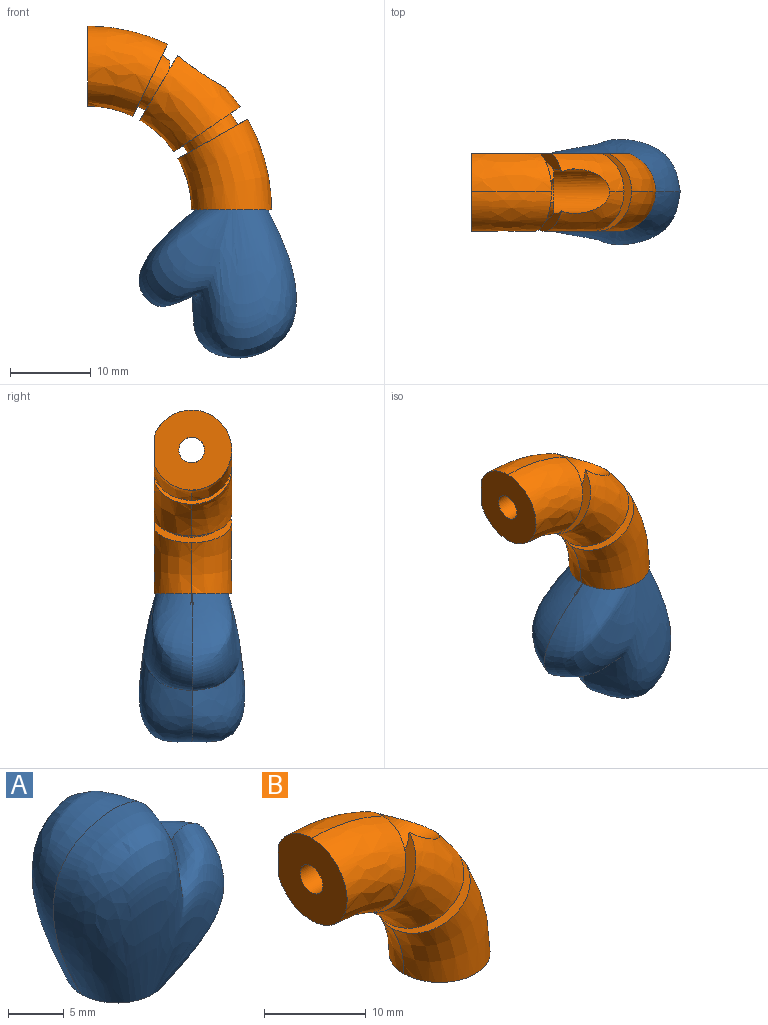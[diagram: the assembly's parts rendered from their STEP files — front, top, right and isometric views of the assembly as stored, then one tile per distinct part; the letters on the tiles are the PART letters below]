
ASSEMBLY  parts=2 mates=1
PART A: 3 faces, bbox 23.5x20.6x22.4 mm
  f0: plane 12.96x12.96mm, normal (0,0,-1), area 63.6mm2, adj f1,f2
  f1: bspline ~19.52x18.47mm, area 451.4mm2, adj f0,f2
  f2: bspline ~19.52x18.47mm, area 451.4mm2, adj f0,f1
PART B: 25 faces, bbox 23x10.6x23 mm
  f0: bspline ~6.94x4.57mm, area 13.1mm2, adj f1,f2,f5,f6,f24
  f1: bspline ~6.94x4.57mm, area 13.1mm2, adj f0,f2,f5,f6,f24
  f2: cylinder r=1.59mm len=10.16mm, axis (-1,0,0), area 98.8mm2, adj f0,f1,f5,f14,f24
  f3: bspline ~9.44x9.13mm, area 38.1mm2, adj f5,f14,f18,f20
  f4: bspline ~9.89x5.21mm, area 58.9mm2, adj f5,f14,f18,f20
  f5: plane 9.88x9.16mm, normal (0.9,0,-0.43), area 36.6mm2, adj f0,f1,f2,f3,f4,f18,f20
  f6: plane 9.65x8.06mm, normal (-0.86,0,0.5), area 28.7mm2, adj f0,f1,f7,f8,f17,f22,f23,f24
  f7: bspline ~6.89x6.74mm, area 38.1mm2, adj f6,f9,f17,f22
  f8: bspline ~9.05x8.75mm, area 41.3mm2, adj f6,f9,f17,f22,f23
  f9: plane 9.68x8.24mm, normal (0.56,0,-0.83), area 36.8mm2, adj f7,f8,f16,f17,f19,f22
  f10: plane 9.64x8.65mm, normal (-0.49,0,0.87), area 36.8mm2, adj f11,f12,f15,f16,f19,f21
  f11: bspline ~7.96x4.95mm, area 43.8mm2, adj f10,f13,f15,f21
  f12: bspline ~11.24x8.32mm, area 67.7mm2, adj f10,f13,f15,f21
  f13: plane 9.93x9.67mm, normal (0,0,-1), area 76.6mm2, adj f11,f12,f15,f21
  f14: plane 9.93x9.63mm, normal (-1,0,0), area 68.7mm2, adj f2,f3,f4,f18,f20
  f15: bspline ~11.6x11.25mm, area 143.3mm2, adj f10,f11,f12,f13
  f16: bspline ~6.78x4.94mm, area 15.7mm2, adj f9,f10,f19
  f17: bspline ~12.48x12.4mm, area 107.1mm2, adj f6,f7,f8,f9,f23
  f18: bspline ~11.19x9.89mm, area 124.6mm2, adj f3,f4,f5,f14
  f19: bspline ~6.78x4.94mm, area 15.7mm2, adj f9,f10,f16
  f20: plane 8.48x5mm, normal (0,1,0), area 27.1mm2, adj f3,f4,f5,f14
  f21: plane 9.64x5.5mm, normal (0,1,0), area 31.1mm2, adj f10,f11,f12,f13
  f22: plane 8.06x7.84mm, normal (0,1,0), area 27.1mm2, adj f6,f7,f8,f9
  f23: cylinder r=2.76mm len=6.93mm, axis (1,0,0), area 43.4mm2, adj f6,f8,f17,f24
  f24: plane 5.54x3.48mm, normal (1,0,0), area 8.3mm2, adj f0,f1,f2,f6,f23
PLACE A rot(axis=(0,-1,0),180deg) t=(5.5,-11.09,-5.06)mm
PLACE B t=(-12.33,-11.04,12.77)mm
MATE fastened A.f0 <-> B.f13  axis (0,0,1) through (5.5,-11.09,-5.06)mm
